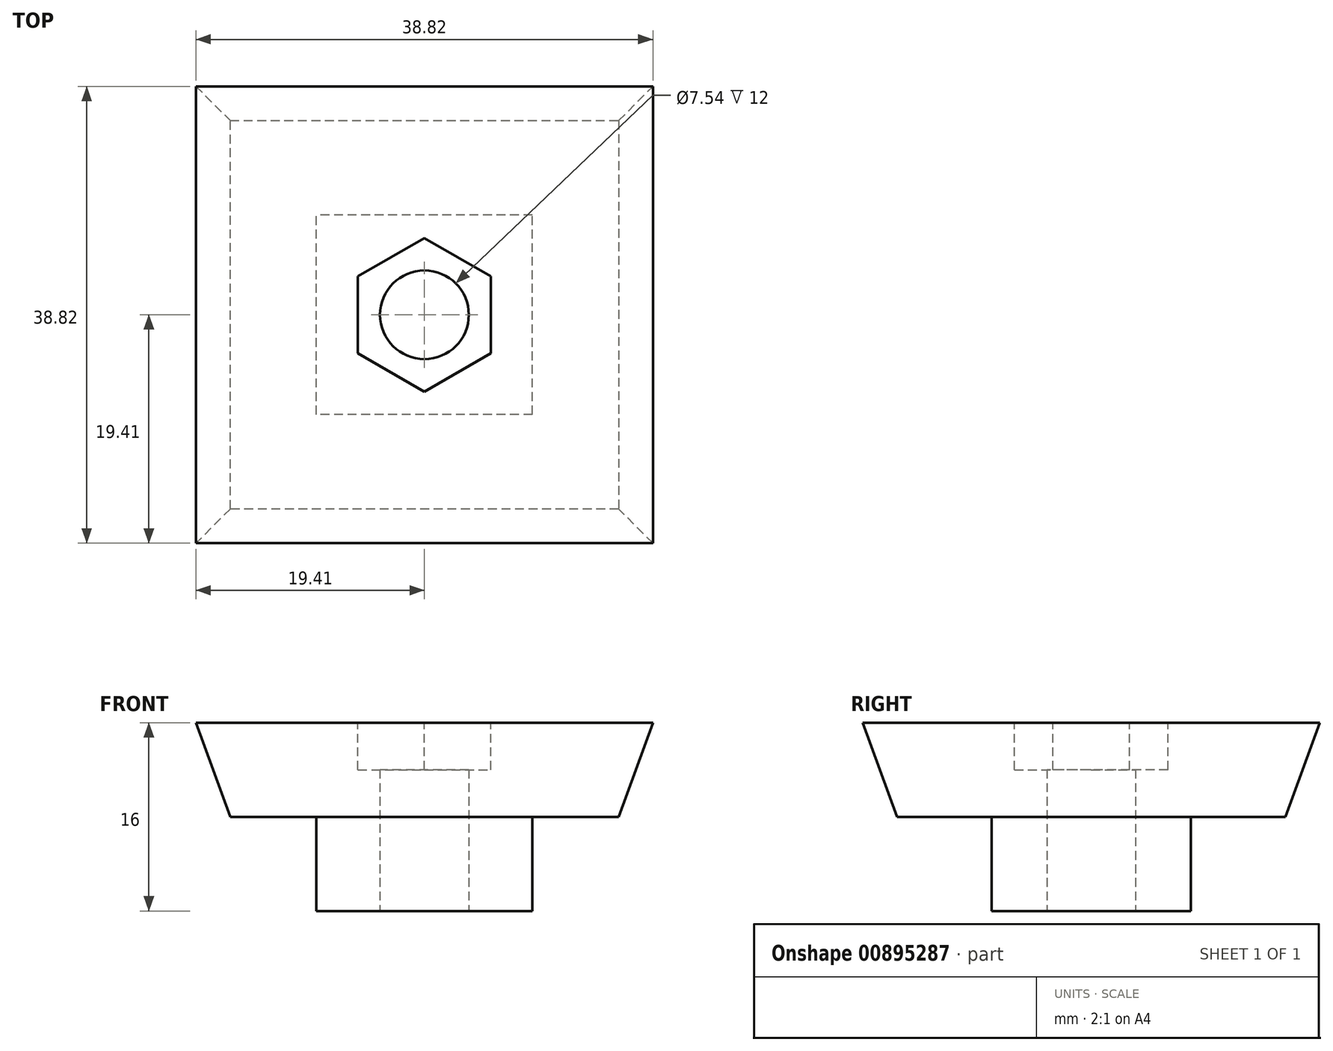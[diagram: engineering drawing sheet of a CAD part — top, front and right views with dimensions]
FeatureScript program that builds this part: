
annotation { "Feature Type Name" : "Feature", "Feature Type Description" : "" }
export const myFeature = defineFeature(function(context is Context, id is Id, definition is map)
    precondition{}
    {
        {
            var Q0;
            Q0=qCreatedBy(makeId("Top.planeOp"),FACE);
            var sketch = newSketch(context, id + "F0", { "sketchPlane" : qUnion([Q0])});
            skLineSegment(sketch, "E0.bottom", {"start": v(16.5, 16.5) * mm, "end": v(-16.5, 16.5) * mm});
            skLineSegment(sketch, "E0.top", {"start": v(16.5, -16.5) * mm, "end": v(-16.5, -16.5) * mm});
            skLineSegment(sketch, "E0.left", {"start": v(16.5, 16.5) * mm, "end": v(16.5, -16.5) * mm});
            skLineSegment(sketch, "E0.right", {"start": v(-16.5, 16.5) * mm, "end": v(-16.5, -16.5) * mm});
            skPoint(sketch, "E0.middle", {"position": v(0, 0) * mm});
            skSolve(sketch);
        }
        {
            var Q0;
            Q0=makeQuery(id+"F0.imprint","IMPRINT",FACE,{"disambiguationData":[TD([[makeQuery(id+"F0.imprint","IMPRINT",EDGE,{"derivedFrom":sQuery(id+"F0.wireOp",EDGE,"E0.bottom")}),1.0]])]});
            extrude(context, id + "F1", {"entities" : qUnion([Q0]), "depth" : 8 * mm, "offsetDistance" : 25 * mm, "hasDraft" : true, "draftAngle" : 20 * degree});
        }
        {
            var Q0;
            Q0=makeQuery(id+"F1.opExtrude","CAP_FACE",FACE,{"disambiguationData":[OSD([sQuery(id+"F0.wireOp",EDGE,"E0.bottom"),sQuery(id+"F0.wireOp",EDGE,"E0.top"),sQuery(id+"F0.wireOp",EDGE,"E0.left"),sQuery(id+"F0.wireOp",EDGE,"E0.right")])],"isStart":false});
            var sketch = newSketch(context, id + "F2", { "sketchPlane" : qUnion([Q0])});
            skCircle(sketch, "E1.cCircle", {"center": v(0, 0) * mm, "radius": 5.65 * mm, "construction": true});
            skLineSegment(sketch, "E1.0", {"start": v(5.65, 3.26) * mm, "end": v(5.65, -3.26) * mm});
            skLineSegment(sketch, "E1.1", {"start": v(5.65, -3.26) * mm, "end": v(0, -6.52) * mm});
            skLineSegment(sketch, "E1.2", {"start": v(0, -6.52) * mm, "end": v(-5.65, -3.26) * mm});
            skLineSegment(sketch, "E1.3", {"start": v(-5.65, -3.26) * mm, "end": v(-5.65, 3.26) * mm});
            skLineSegment(sketch, "E1.4", {"start": v(-5.65, 3.26) * mm, "end": v(0, 6.52) * mm});
            skLineSegment(sketch, "E1.5", {"start": v(0, 6.52) * mm, "end": v(5.65, 3.26) * mm});
            skPoint(sketch, "E1.0.midPoint", {"position": v(5.65, 0) * mm});
            skSolve(sketch);
        }
        {
            var Q0;
            Q0 = qSketchRegion(id + "F2", true);
            extrude(context, id + "F3", {"entities" : qUnion([Q0]), "operationType" : NewBodyOperationType.REMOVE, "oppositeDirection" : true, "depth" : 4 * mm, "offsetDistance" : 25 * mm});
        }
        {
            var Q0;
            Q0=makeQuery(id+"F1.opExtrude","CAP_FACE",FACE,{"disambiguationData":[OSD([sQuery(id+"F0.wireOp",EDGE,"E0.bottom"),sQuery(id+"F0.wireOp",EDGE,"E0.top"),sQuery(id+"F0.wireOp",EDGE,"E0.left"),sQuery(id+"F0.wireOp",EDGE,"E0.right")])],"isStart":true});
            var sketch = newSketch(context, id + "F4", { "sketchPlane" : qUnion([Q0])});
            skLineSegment(sketch, "E2.bottom", {"start": v(9.18, 8.47) * mm, "end": v(-9.18, 8.47) * mm});
            skLineSegment(sketch, "E2.top", {"start": v(9.18, -8.47) * mm, "end": v(-9.18, -8.47) * mm});
            skLineSegment(sketch, "E2.left", {"start": v(9.18, 8.47) * mm, "end": v(9.18, -8.47) * mm});
            skLineSegment(sketch, "E2.right", {"start": v(-9.18, 8.47) * mm, "end": v(-9.18, -8.47) * mm});
            skPoint(sketch, "E2.middle", {"position": v(0, 0) * mm});
            skSolve(sketch);
        }
        {
            var Q0;
            Q0 = qSketchRegion(id + "F4", true);
            extrude(context, id + "F5", {"entities" : qUnion([Q0]), "operationType" : NewBodyOperationType.ADD, "depth" : 8 * mm, "offsetDistance" : 25 * mm});
        }
        {
            var Q0;
            Q0=makeQuery(id+"F5.opExtrude","CAP_FACE",FACE,{"disambiguationData":[OSD([sQuery(id+"F4.wireOp",EDGE,"E2.bottom"),sQuery(id+"F4.wireOp",EDGE,"E2.top"),sQuery(id+"F4.wireOp",EDGE,"E2.left"),sQuery(id+"F4.wireOp",EDGE,"E2.right")])],"isStart":false});
            var sketch = newSketch(context, id + "F6", { "sketchPlane" : qUnion([Q0])});
            skPoint(sketch, "E3", {"position": v(0, 0) * mm});
            skSolve(sketch);
        }
        {
            var Q0;
            Q0=sQuery(id+"F6.wireOp",VERTEX,"E3");
            var Q1;
            Q1=makeQuery(id+"F1.opExtrude","SWEPT_BODY",BODY,{"disambiguationData":[OSD([sQuery(id+"F0.wireOp",EDGE,"E0.bottom"),sQuery(id+"F0.wireOp",EDGE,"E0.top"),sQuery(id+"F0.wireOp",EDGE,"E0.left"),sQuery(id+"F0.wireOp",EDGE,"E0.right")])]});
            hole(context, id + "F7", {"style" : HoleStyle.SIMPLE, "endStyle" : HoleEndStyle.BLIND, "standardTappedOrClearance" : lookupTablePath({ "fit" : "Loose (ASME)", "standard" : "ANSI", "size" : "1/4", "type" : "Clearance" }), "standardBlindInLast" : lookupTablePath({ "fit" : "Loose", "standard" : "ANSI", "size" : "1/4", "type" : "Clearance" }), "holeDiameter" : 7.54 * mm, "majorDiameter" : 5 * mm, "holeDepth" : 25 * mm, "isTappedThrough" : true, "tappedDepth" : 12 * mm, "tapClearance" : 3, "startFromSketch" : true, "locations" : qUnion([Q0]), "scope" : qUnion([Q1])});
        }
    });
